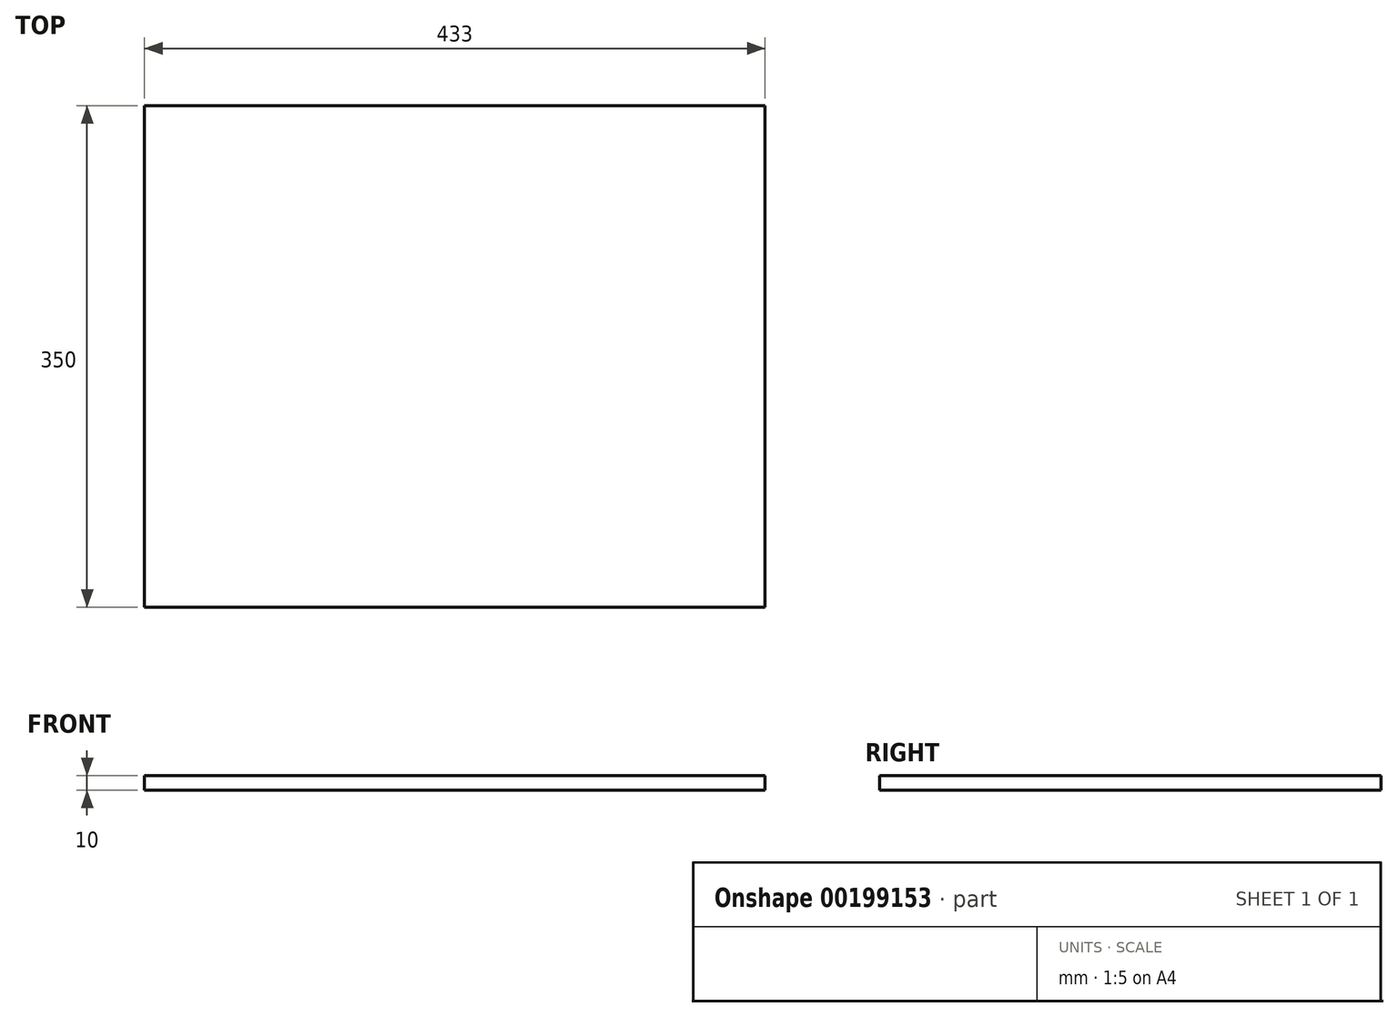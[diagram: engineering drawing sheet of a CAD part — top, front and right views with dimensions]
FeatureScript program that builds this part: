
annotation { "Feature Type Name" : "Feature", "Feature Type Description" : "" }
export const myFeature = defineFeature(function(context is Context, id is Id, definition is map)
    precondition{}
    {
        {
            var Q0;
            Q0=qCreatedBy(makeId("Top.planeOp"),FACE);
            var sketch = newSketch(context, id + "F0", { "sketchPlane" : qUnion([Q0])});
            skLineSegment(sketch, "E0.bottom", {"start": v(-70.96, 65.05) * mm, "end": v(362.04, 65.05) * mm});
            skLineSegment(sketch, "E0.top", {"start": v(-70.96, -284.95) * mm, "end": v(362.04, -284.95) * mm});
            skLineSegment(sketch, "E0.left", {"start": v(-70.96, 65.05) * mm, "end": v(-70.96, -284.95) * mm});
            skLineSegment(sketch, "E0.right", {"start": v(362.04, 65.05) * mm, "end": v(362.04, -284.95) * mm});
            skSolve(sketch);
        }
        {
            var Q0;
            Q0=qSketchRegion(id+"F0",true);
            extrude(context, id + "F1", {"entities" : qUnion([Q0]), "depth" : 10 * mm});
        }
    });
